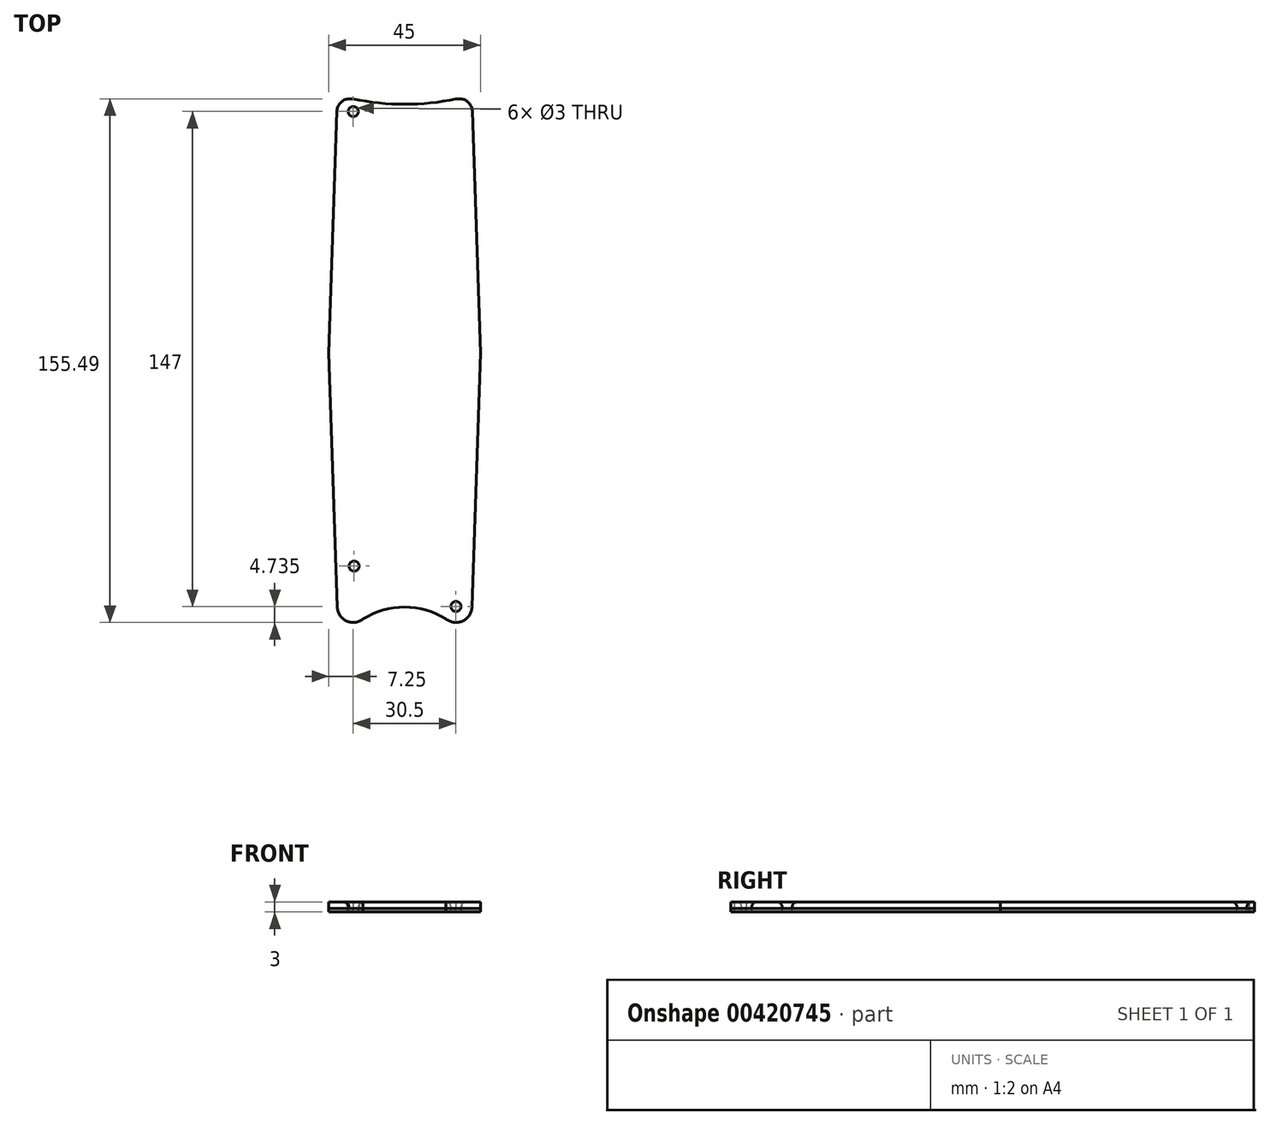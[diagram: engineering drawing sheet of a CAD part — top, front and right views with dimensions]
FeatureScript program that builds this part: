
annotation { "Feature Type Name" : "Feature", "Feature Type Description" : "" }
export const myFeature = defineFeature(function(context is Context, id is Id, definition is map)
    precondition{}
    {
        {
            var Q0;
            Q0=qCreatedBy(makeId("Top.planeOp"),FACE);
            var sketch = newSketch(context, id + "F0", { "sketchPlane" : qUnion([Q0])});
            skLineSegment(sketch, "E0", {"start": v(0, 0) * mm, "end": v(0, 131.9) * mm, "construction": true});
            skLineSegment(sketch, "E1", {"start": v(0, 131.9) * mm, "end": v(0, -166.71) * mm, "construction": true});
            skLineSegment(sketch, "E2", {"start": v(-0.13, 78.3) * mm, "end": v(-0.13, 40.94) * mm, "construction": true});
            skLineSegment(sketch, "E3", {"start": v(-80.95, 4.44) * mm, "end": v(-22.63, 4.44) * mm, "construction": true});
            skLineSegment(sketch, "E4", {"start": v(-20.24, 76.14) * mm, "end": v(-22.63, 4.44) * mm});
            skLineSegment(sketch, "E5", {"start": v(-17.13, 79.9) * mm, "end": v(-15.38, 79.9) * mm});
            skLineSegment(sketch, "E6", {"start": v(-0.13, 78.3) * mm, "end": v(-0.13, 36.94) * mm});
            skLineSegment(sketch, "E7.MirrorCS", {"start": v(19.98, 76.14) * mm, "end": v(22.37, 4.44) * mm});
            skLineSegment(sketch, "E8.MirrorCS", {"start": v(16.87, 79.9) * mm, "end": v(15.12, 79.9) * mm});
            skLineSegment(sketch, "E9.MirrorCS", {"start": v(-0.13, 36.94) * mm, "end": v(0, 36.94) * mm});
            skLineSegment(sketch, "E10.MirrorCS", {"start": v(-20.11, -71.02) * mm, "end": v(-22.63, 4.44) * mm});
            skLineSegment(sketch, "E11.MirrorCS", {"start": v(19.85, -71.02) * mm, "end": v(22.37, 4.44) * mm});
            skLineSegment(sketch, "E12.MirrorCS", {"start": v(-0.13, -28.06) * mm, "end": v(0, -28.06) * mm});
            skLineSegment(sketch, "E13.trimOffspring", {"start": v(-0.13, -28.06) * mm, "end": v(-0.13, -80.04) * mm, "construction": true});
            skLineSegment(sketch, "E14.trimOffspring", {"start": v(18.37, 4.44) * mm, "end": v(98.23, 4.44) * mm, "construction": true});
            skCircle(sketch, "E15", {"center": v(-15.38, -70.86) * mm, "radius": 1.5 * mm});
            skCircle(sketch, "E16.MirrorC", {"center": v(15.12, -70.86) * mm, "radius": 1.5 * mm});
            skCircle(sketch, "E17", {"center": v(15.12, 76.14) * mm, "radius": 1.5 * mm});
            skCircle(sketch, "E18.MirrorC", {"center": v(-15.38, 76.14) * mm, "radius": 1.5 * mm});
            skCircle(sketch, "E19", {"center": v(14.87, -58.86) * mm, "radius": 1.5 * mm});
            skCircle(sketch, "E20.MirrorC", {"center": v(-15.13, -58.86) * mm, "radius": 1.5 * mm});
            skArc(sketch, "E21", {"start": v(0, 40.93) * mm, "mid": v(-0.07, 40.94) * mm, "end": v(-0.13, 40.94) * mm});
            skArc(sketch, "E22", {"start": v(-20.11, -71.02) * mm, "mid": v(-17.37, -75.16) * mm, "end": v(-12.44, -74.58) * mm});
            skArc(sketch, "E23.MirrorCS", {"start": v(19.85, -71.02) * mm, "mid": v(17.11, -75.16) * mm, "end": v(12.18, -74.58) * mm});
            skPoint(sketch, "E24.trimOffspring.end.orphan", {"position": v(-0.13, -71.02) * mm});
            skArc(sketch, "E25", {"start": v(12.18, -74.58) * mm, "mid": v(-0.13, -71.02) * mm, "end": v(-12.44, -74.58) * mm});
            skArc(sketch, "E26", {"start": v(19.98, 76.14) * mm, "mid": v(18.43, 79.16) * mm, "end": v(15.12, 79.9) * mm});
            skArc(sketch, "E27.MirrorCS", {"start": v(-20.24, 76.14) * mm, "mid": v(-18.7, 79.16) * mm, "end": v(-15.38, 79.9) * mm});
            skArc(sketch, "E28", {"start": v(-15.38, 79.9) * mm, "mid": v(-0.13, 78.3) * mm, "end": v(15.12, 79.9) * mm});
            skPoint(sketch, "E29.orphan", {"position": v(-0.13, 79.9) * mm});
            skPoint(sketch, "E30.orphan", {"position": v(-0.13, 79.09) * mm});
            skPoint(sketch, "E31.orphan", {"position": v(-18.63, 4.44) * mm});
            skPoint(sketch, "E32.MirrorCS.start.orphan", {"position": v(-11.63, -28.06) * mm});
            skPoint(sketch, "E33.end.orphan", {"position": v(-21.54, -28.16) * mm});
            skPoint(sketch, "E34.MirrorCS.end.orphan", {"position": v(-18.63, -21.06) * mm});
            skPoint(sketch, "E35.orphan", {"position": v(-18.63, -28.06) * mm});
            skPoint(sketch, "E36.orphan", {"position": v(-0.13, -28.06) * mm});
            skPoint(sketch, "E37.end.orphan", {"position": v(-18.63, 29.94) * mm});
            skPoint(sketch, "E38.orphan", {"position": v(18.37, 4.44) * mm});
            skPoint(sketch, "E39.MirrorCS.end.orphan", {"position": v(18.37, -21.06) * mm});
            skPoint(sketch, "E39.MirrorCS.start.orphan", {"position": v(18.37, -28.06) * mm});
            skPoint(sketch, "E40.center.orphan", {"position": v(-16.63, 34.94) * mm});
            skPoint(sketch, "E41.trimOffspring.end.orphan", {"position": v(-18.63, 36.94) * mm});
            skPoint(sketch, "E41.trimOffspring.start.orphan", {"position": v(-11.63, 36.94) * mm});
            skPoint(sketch, "E42.trimOffspring.end.orphan", {"position": v(18.37, 36.94) * mm});
            skPoint(sketch, "E42.trimOffspring.start.orphan", {"position": v(11.37, 36.94) * mm});
            skPoint(sketch, "E43.MirrorCS.end.orphan", {"position": v(18.37, 29.94) * mm});
            skPoint(sketch, "E44.MirrorCS.end.orphan", {"position": v(21.28, -28.16) * mm});
            skPoint(sketch, "E45.trimOffspring.end.orphan", {"position": v(13.92, -28.06) * mm});
            skPoint(sketch, "E45.trimOffspring.start.orphan", {"position": v(11.37, -28.06) * mm});
            skPoint(sketch, "E46.MirrorCS.end.orphan", {"position": v(-14.18, -28.06) * mm});
            skPoint(sketch, "E47.start.orphan", {"position": v(-14.18, -68.42) * mm});
            skPoint(sketch, "E48.end.orphan", {"position": v(-17.72, -74.99) * mm});
            skPoint(sketch, "E48.start.orphan", {"position": v(-17.72, -69.47) * mm});
            skPoint(sketch, "E49.MirrorCS.end.orphan", {"position": v(17.46, -74.99) * mm});
            skPoint(sketch, "E49.MirrorCS.start.orphan", {"position": v(17.46, -69.47) * mm});
            skPoint(sketch, "E50.MirrorCS.start.orphan", {"position": v(13.92, -68.42) * mm});
            skPoint(sketch, "E51.orphan", {"position": v(-20.11, 79.9) * mm});
            skPoint(sketch, "E52.orphan", {"position": v(19.85, 79.9) * mm});
            skSolve(sketch);
        }
        {
            var Q0;
            Q0=makeQuery(id+"F0.imprint","IMPRINT",FACE,{"disambiguationData":[TD([[makeQuery(id+"F0.imprint","IMPRINT",EDGE,{"derivedFrom":sQuery(id+"F0.wireOp",EDGE,"E16.MirrorC")}),-1.0]])]});
            var Q1;
            Q1=makeQuery(id+"F0.imprint","IMPRINT",FACE,{"disambiguationData":[TD([[makeQuery(id+"F0.imprint","IMPRINT",EDGE,{"derivedFrom":sQuery(id+"F0.wireOp",EDGE,"E19")}),1.0]])]});
            var Q2;
            Q2=makeQuery(id+"F0.imprint","IMPRINT",FACE,{"disambiguationData":[TD([[makeQuery(id+"F0.imprint","IMPRINT",EDGE,{"derivedFrom":sQuery(id+"F0.wireOp",EDGE,"E15")}),1.0]])]});
            var Q3;
            Q3=makeQuery(id+"F0.imprint","IMPRINT",FACE,{"disambiguationData":[TD([[makeQuery(id+"F0.imprint","IMPRINT",EDGE,{"derivedFrom":sQuery(id+"F0.wireOp",EDGE,"E20.MirrorC")}),-1.0]])]});
            var Q4;
            Q4=makeQuery(id+"F0.imprint","IMPRINT",FACE,{"disambiguationData":[TD([[makeQuery(id+"F0.imprint","IMPRINT",EDGE,{"derivedFrom":sQuery(id+"F0.wireOp",EDGE,"E17")}),1.0]])]});
            var Q5;
            Q5=makeQuery(id+"F0.imprint","IMPRINT",FACE,{"disambiguationData":[TD([[makeQuery(id+"F0.imprint","IMPRINT",EDGE,{"derivedFrom":sQuery(id+"F0.wireOp",EDGE,"E18.MirrorC")}),-1.0]])]});
            extrude(context, id + "F1", {"entities" : qUnion([Q0, Q1, Q2, Q3, Q4, Q5]), "depth" : 2 * mm, "offsetDistance" : 25 * mm});
        }
        {
            var Q0;
            {var subQ0=sQuery(id+"F0.wireOp",EDGE,"E4");Q0=makeQuery(id+"F0.imprint","IMPRINT",FACE,{"disambiguationData":[TD([[makeQuery(id+"F0.imprint","IMPRINT",EDGE,{"derivedFrom":subQ0}),1.0]])]});}
            var Q1;
            Q1=makeQuery(id+"F0.imprint","IMPRINT",FACE,{"disambiguationData":[TD([[makeQuery(id+"F0.imprint","IMPRINT",EDGE,{"derivedFrom":sQuery(id+"F0.wireOp",EDGE,"E20.MirrorC")}),-1.0]])]});
            var Q2;
            Q2=makeQuery(id+"F0.imprint","IMPRINT",FACE,{"disambiguationData":[TD([[makeQuery(id+"F0.imprint","IMPRINT",EDGE,{"derivedFrom":sQuery(id+"F0.wireOp",EDGE,"E15")}),1.0]])]});
            var Q3;
            Q3=makeQuery(id+"F0.imprint","IMPRINT",FACE,{"disambiguationData":[TD([[makeQuery(id+"F0.imprint","IMPRINT",EDGE,{"derivedFrom":sQuery(id+"F0.wireOp",EDGE,"E16.MirrorC")}),-1.0]])]});
            var Q4;
            Q4=makeQuery(id+"F0.imprint","IMPRINT",FACE,{"disambiguationData":[TD([[makeQuery(id+"F0.imprint","IMPRINT",EDGE,{"derivedFrom":sQuery(id+"F0.wireOp",EDGE,"E19")}),1.0]])]});
            var Q5;
            Q5=makeQuery(id+"F0.imprint","IMPRINT",FACE,{"disambiguationData":[TD([[makeQuery(id+"F0.imprint","IMPRINT",EDGE,{"derivedFrom":sQuery(id+"F0.wireOp",EDGE,"E17")}),1.0]])]});
            var Q6;
            Q6=makeQuery(id+"F0.imprint","IMPRINT",FACE,{"disambiguationData":[TD([[makeQuery(id+"F0.imprint","IMPRINT",EDGE,{"derivedFrom":sQuery(id+"F0.wireOp",EDGE,"E18.MirrorC")}),-1.0]])]});
            extrude(context, id + "F2", {"entities" : qUnion([Q0, Q1, Q2, Q3, Q4, Q5, Q6]), "oppositeDirection" : true, "depth" : 1 * mm, "offsetDistance" : 25 * mm});
        }
        {
            var Q0;
            Q0=makeQuery(id+"F1.opExtrude","CAP_EDGE",EDGE,{"disambiguationData":[OSD([sQuery(id+"F0.wireOp",EDGE,"E17")])],"isStart":false});
            var Q1;
            Q1=makeQuery(id+"F1.opExtrude","CAP_EDGE",EDGE,{"disambiguationData":[OSD([sQuery(id+"F0.wireOp",EDGE,"E18.MirrorC")])],"isStart":false});
            var Q2;
            Q2=makeQuery(id+"F1.opExtrude","CAP_EDGE",EDGE,{"disambiguationData":[OSD([sQuery(id+"F0.wireOp",EDGE,"E19")])],"isStart":false});
            var Q3;
            Q3=makeQuery(id+"F1.opExtrude","CAP_EDGE",EDGE,{"disambiguationData":[OSD([sQuery(id+"F0.wireOp",EDGE,"E16.MirrorC")])],"isStart":false});
            var Q4;
            Q4=makeQuery(id+"F1.opExtrude","CAP_EDGE",EDGE,{"disambiguationData":[OSD([sQuery(id+"F0.wireOp",EDGE,"E20.MirrorC")])],"isStart":false});
            var Q5;
            Q5=makeQuery(id+"F1.opExtrude","CAP_EDGE",EDGE,{"disambiguationData":[OSD([sQuery(id+"F0.wireOp",EDGE,"E15")])],"isStart":false});
            fillet(context, id + "F3", {"entities" : qUnion([Q0, Q1, Q2, Q3, Q4, Q5]), "radius" : 1.5 * mm, "tangentPropagation" : true, "allowEdgeOverflow" : false});
        }
        {
            var Q0;
            Q0=qCreatedBy(makeId("Right.planeOp"),FACE);
            cPlane(context, id + "F4", {"entities" : qUnion([Q0]), "cplaneType" : CPlaneType.OFFSET, "offset" : 15.1 * mm, "width" : 150 * mm, "height" : 150 * mm});
        }
    });
